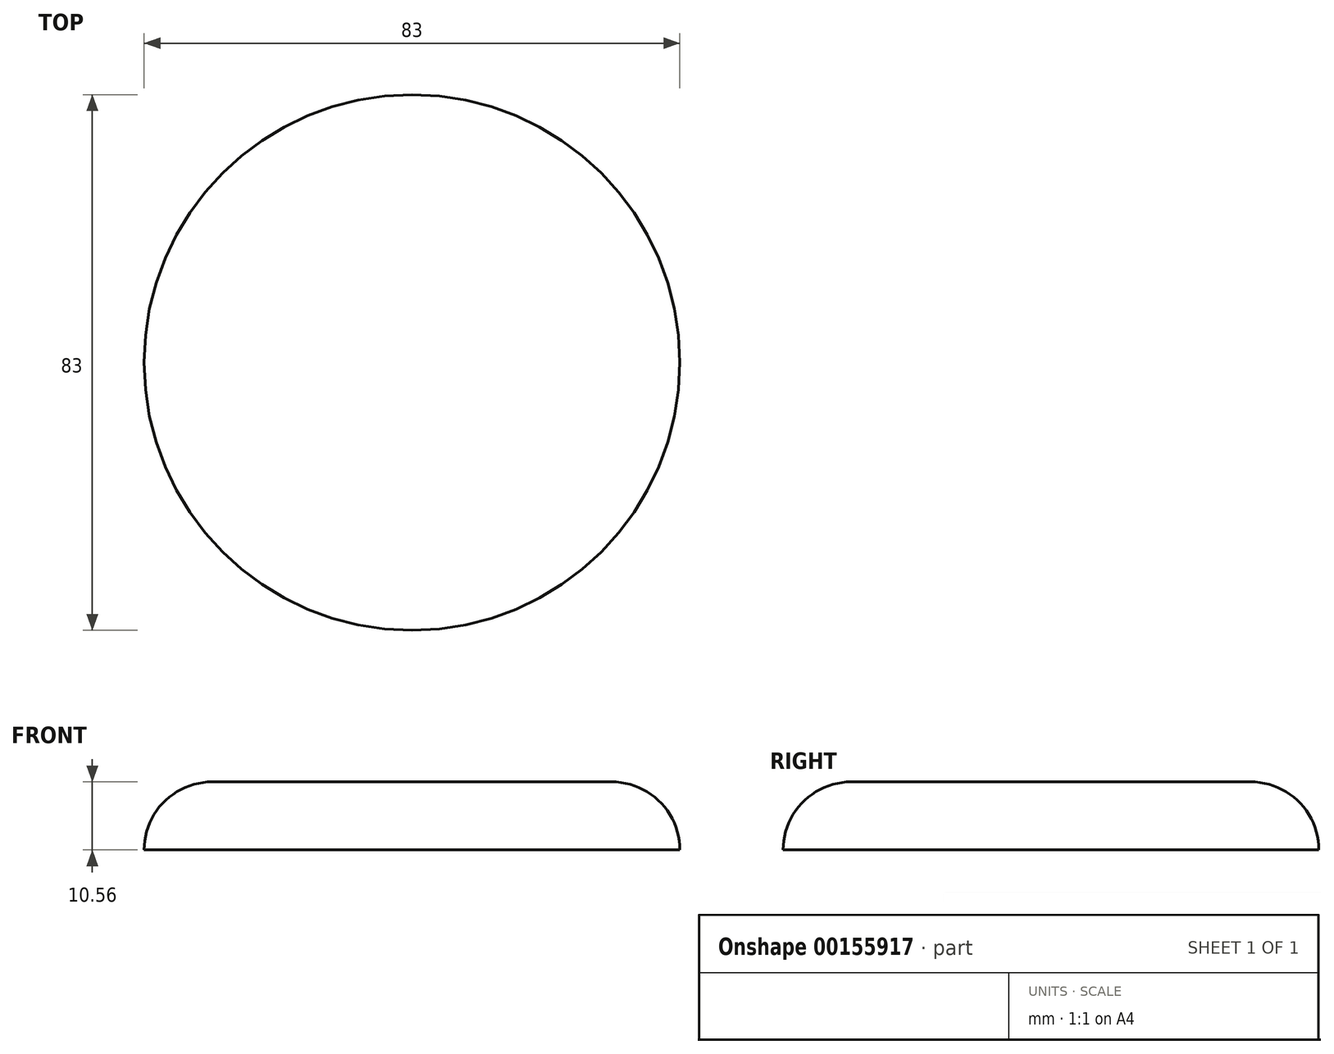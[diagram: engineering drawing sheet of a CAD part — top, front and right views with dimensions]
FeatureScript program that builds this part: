
annotation { "Feature Type Name" : "Feature", "Feature Type Description" : "" }
export const myFeature = defineFeature(function(context is Context, id is Id, definition is map)
    precondition{}
    {
        {
            var Q0;
            Q0=qCreatedBy(makeId("Front.planeOp"),FACE);
            var sketch = newSketch(context, id + "F0", { "sketchPlane" : qUnion([Q0])});
            skLineSegment(sketch, "E0", {"start": v(-41.5, 0) * mm, "end": v(0, 0) * mm});
            skLineSegment(sketch, "E1", {"start": v(0, 0) * mm, "end": v(0, 10.56) * mm});
            skLineSegment(sketch, "E2", {"start": v(0, 10.56) * mm, "end": v(-30.94, 10.56) * mm});
            skArc(sketch, "E3", {"start": v(-30.94, 10.56) * mm, "mid": v(-38.4, 7.47) * mm, "end": v(-41.5, 0) * mm});
            skSolve(sketch);
        }
        {
            var Q0;
            Q0 = qSketchRegion(id + "F0", true);
            var Q1;
            Q1=sQuery(id+"F0.wireOp",EDGE,"E1");
            revolve(context, id + "F1", {"entities" : qUnion([Q0]), "axis" : qUnion([Q1]), "revolveType" : RevolveType.FULL});
        }
    });
